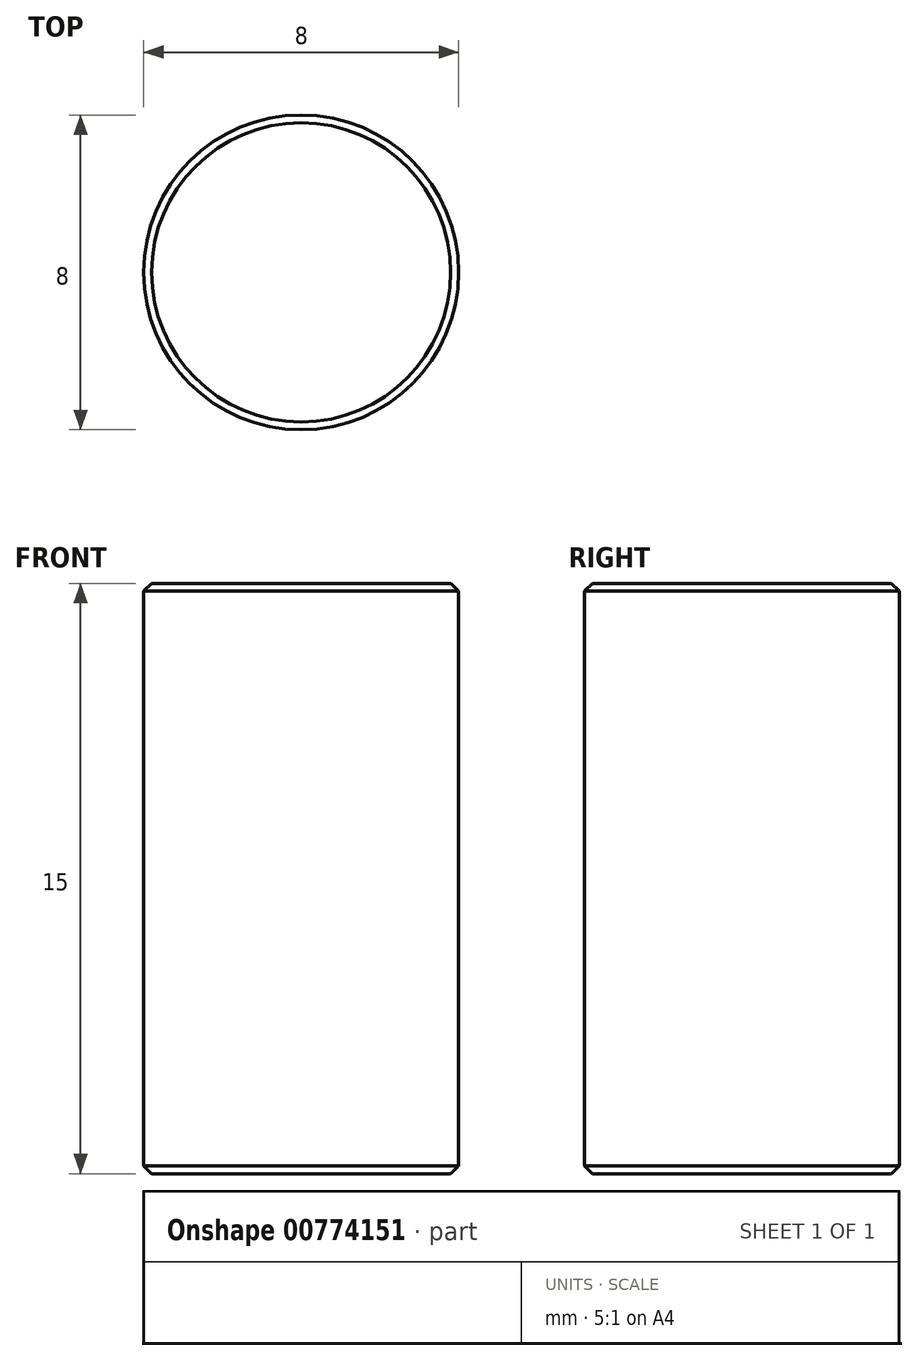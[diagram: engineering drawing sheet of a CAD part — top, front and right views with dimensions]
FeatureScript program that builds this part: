
annotation { "Feature Type Name" : "Feature", "Feature Type Description" : "" }
export const myFeature = defineFeature(function(context is Context, id is Id, definition is map)
    precondition{}
    {
        {
            var Q0;
            Q0=qCreatedBy(makeId("Top.planeOp"),FACE);
            var sketch = newSketch(context, id + "F0", { "sketchPlane" : qUnion([Q0])});
            skCircle(sketch, "E0", {"center": v(0, 0) * mm, "radius": 4 * mm});
            skSolve(sketch);
        }
        {
            var Q0;
            Q0=makeQuery(id+"F0.imprint","IMPRINT",FACE,{"disambiguationData":[TD([[makeQuery(id+"F0.imprint","IMPRINT",EDGE,{"derivedFrom":sQuery(id+"F0.wireOp",EDGE,"E0")}),1.0]])]});
            extrude(context, id + "F1", {"entities" : qUnion([Q0]), "depth" : 15 * mm, "offsetDistance" : 25 * mm});
        }
        {
            var Q0;
            Q0=makeQuery(id+"F1.opExtrude","CAP_EDGE",EDGE,{"disambiguationData":[OSD([sQuery(id+"F0.wireOp",EDGE,"E0")])],"isStart":false});
            chamfer(context, id + "F2", {"entities" : qUnion([Q0]), "width" : 0.2 * mm, "tangentPropagation" : true});
        }
        {
            var Q0;
            Q0=makeQuery(id+"F1.opExtrude","CAP_EDGE",EDGE,{"disambiguationData":[OSD([sQuery(id+"F0.wireOp",EDGE,"E0")])],"isStart":true});
            chamfer(context, id + "F3", {"entities" : qUnion([Q0]), "width" : 0.2 * mm, "tangentPropagation" : true});
        }
    });
